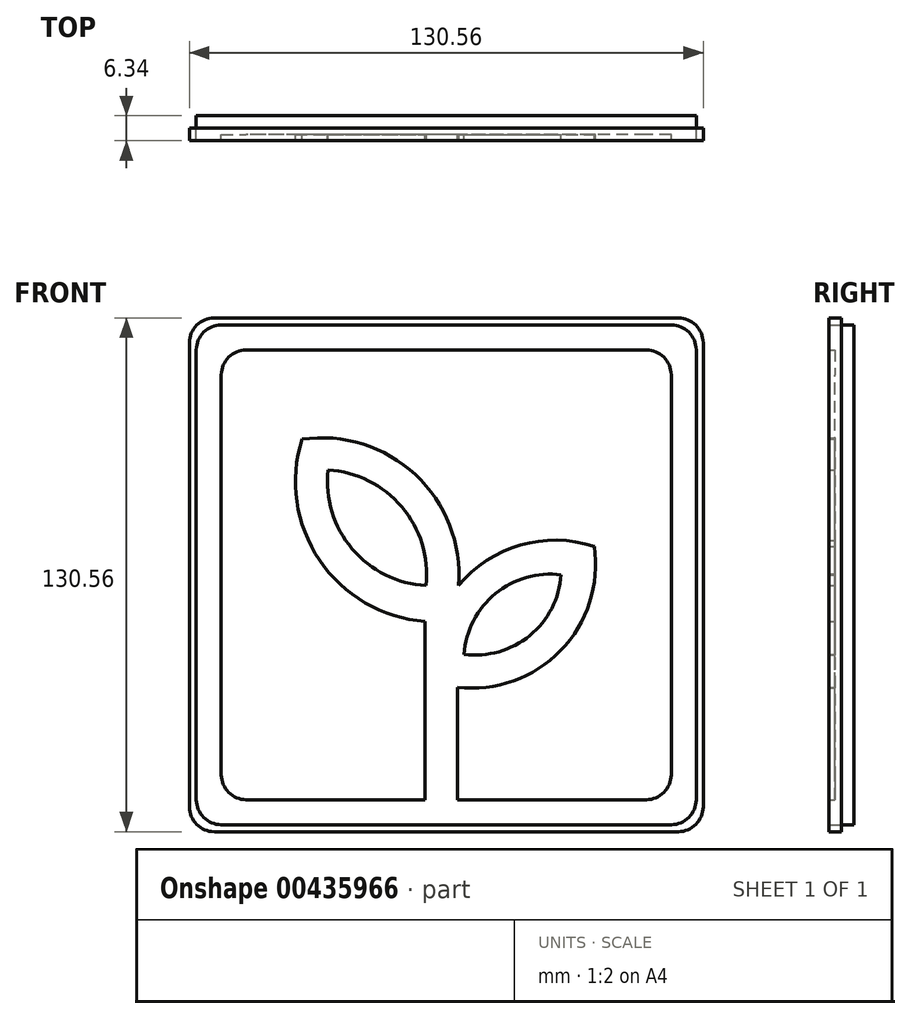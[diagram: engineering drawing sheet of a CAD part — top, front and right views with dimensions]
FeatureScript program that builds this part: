
annotation { "Feature Type Name" : "Feature", "Feature Type Description" : "" }
export const myFeature = defineFeature(function(context is Context, id is Id, definition is map)
    precondition{}
    {
        {
            var Q0;
            Q0=qCreatedBy(makeId("Front.planeOp"),FACE);
            var sketch = newSketch(context, id + "F0", { "sketchPlane" : qUnion([Q0])});
            skLineSegment(sketch, "E0", {"start": v(0, 67.9) * mm, "end": v(0, -67.43) * mm, "construction": true});
            skLineSegment(sketch, "E1", {"start": v(-68.62, 0) * mm, "end": v(68.14, 0) * mm, "construction": true});
            skLineSegment(sketch, "E2.bottom", {"start": v(-57.15, 63.5) * mm, "end": v(57.15, 63.5) * mm});
            skLineSegment(sketch, "E2.top", {"start": v(-57.15, -63.5) * mm, "end": v(57.15, -63.5) * mm});
            skLineSegment(sketch, "E2.left", {"start": v(-63.5, 57.15) * mm, "end": v(-63.5, -57.15) * mm});
            skLineSegment(sketch, "E2.right", {"start": v(63.5, 57.15) * mm, "end": v(63.5, -57.15) * mm});
            skPoint(sketch, "E3.visualSharp", {"position": v(-63.5, 63.5) * mm});
            skArc(sketch, "E3.filletArc", {"start": v(-57.15, 63.5) * mm, "mid": v(-61.64, 61.64) * mm, "end": v(-63.5, 57.15) * mm});
            skPoint(sketch, "E4.visualSharp", {"position": v(-63.5, -63.5) * mm});
            skArc(sketch, "E4.filletArc", {"start": v(-63.5, -57.15) * mm, "mid": v(-61.64, -61.64) * mm, "end": v(-57.15, -63.5) * mm});
            skPoint(sketch, "E5.visualSharp", {"position": v(63.5, -63.5) * mm});
            skArc(sketch, "E5.filletArc", {"start": v(57.15, -63.5) * mm, "mid": v(61.64, -61.64) * mm, "end": v(63.5, -57.15) * mm});
            skPoint(sketch, "E6.visualSharp", {"position": v(63.5, 63.5) * mm});
            skArc(sketch, "E6.filletArc", {"start": v(63.5, 57.15) * mm, "mid": v(61.64, 61.64) * mm, "end": v(57.15, 63.5) * mm});
            skSolve(sketch);
        }
        {
            var Q0;
            Q0=makeQuery(id+"F0.imprint","IMPRINT",FACE,{"disambiguationData":[TD([[makeQuery(id+"F0.imprint","IMPRINT",EDGE,{"derivedFrom":sQuery(id+"F0.wireOp",EDGE,"E2.bottom")}),-1.0]])]});
            var sketch = newSketch(context, id + "F1", { "sketchPlane" : qUnion([Q0])});
            skLineSegment(sketch, "E7", {"start": v(-5.39, -57.15) * mm, "end": v(-5.39, -11.84) * mm});
            skArc(sketch, "E8", {"start": v(4.55, -20.2) * mm, "mid": v(21.24, -15.43) * mm, "end": v(29.17, 0) * mm});
            skArc(sketch, "E9", {"start": v(29.17, 0) * mm, "mid": v(12.5, -4.79) * mm, "end": v(4.55, -20.2) * mm});
            skPoint(sketch, "E10", {"position": v(37.6, 7.23) * mm});
            skPoint(sketch, "E11", {"position": v(3.09, -2.73) * mm});
            skPoint(sketch, "E12", {"position": v(-5.1, -2.73) * mm});
            skPoint(sketch, "E13", {"position": v(-36.64, 34.45) * mm});
            skPoint(sketch, "E14", {"position": v(-30.02, 26.63) * mm});
            skArc(sketch, "E15", {"start": v(2.84, -28.56) * mm, "mid": v(29.07, -19.26) * mm, "end": v(37.6, 7.23) * mm});
            skArc(sketch, "E16", {"start": v(37.6, 7.23) * mm, "mid": v(18.83, 7.52) * mm, "end": v(3.09, -2.73) * mm});
            skArc(sketch, "E17", {"start": v(-5.1, -2.73) * mm, "mid": v(-11.3, 17.27) * mm, "end": v(-30.02, 26.63) * mm});
            skArc(sketch, "E18", {"start": v(-30.02, 26.63) * mm, "mid": v(-23.9, 6.59) * mm, "end": v(-5.1, -2.73) * mm});
            skArc(sketch, "E19", {"start": v(-36.64, 34.45) * mm, "mid": v(-32.21, 3.74) * mm, "end": v(-5.39, -11.84) * mm});
            skArc(sketch, "E20", {"start": v(3.09, -2.73) * mm, "mid": v(-7.83, 25.42) * mm, "end": v(-36.64, 34.45) * mm});
            skLineSegment(sketch, "E21.bottom", {"start": v(-50.8, 57.15) * mm, "end": v(50.8, 57.15) * mm});
            skLineSegment(sketch, "E21.top", {"start": v(-50.8, -57.15) * mm, "end": v(-5.39, -57.15) * mm});
            skLineSegment(sketch, "E21.left", {"start": v(-57.15, 50.8) * mm, "end": v(-57.15, -50.8) * mm});
            skLineSegment(sketch, "E21.right", {"start": v(57.15, 50.8) * mm, "end": v(57.15, -50.8) * mm});
            skArc(sketch, "E22.filletArc", {"start": v(-57.15, -50.8) * mm, "mid": v(-55.3, -55.3) * mm, "end": v(-50.8, -57.15) * mm});
            skPoint(sketch, "E23.visualSharp", {"position": v(-57.15, 57.15) * mm});
            skArc(sketch, "E23.filletArc", {"start": v(-50.8, 57.15) * mm, "mid": v(-55.3, 55.3) * mm, "end": v(-57.15, 50.8) * mm});
            skPoint(sketch, "E24.visualSharp", {"position": v(57.15, 57.15) * mm});
            skArc(sketch, "E24.filletArc", {"start": v(57.15, 50.8) * mm, "mid": v(55.3, 55.3) * mm, "end": v(50.8, 57.15) * mm});
            skArc(sketch, "E25.filletArc", {"start": v(50.8, -57.15) * mm, "mid": v(55.3, -55.3) * mm, "end": v(57.15, -50.8) * mm});
            skLineSegment(sketch, "E26", {"start": v(2.84, -28.56) * mm, "end": v(2.84, -57.15) * mm});
            skLineSegment(sketch, "E27.bottom", {"start": v(-58.93, 65.28) * mm, "end": v(58.93, 65.28) * mm});
            skLineSegment(sketch, "E27.top", {"start": v(-58.93, -65.28) * mm, "end": v(58.93, -65.28) * mm});
            skLineSegment(sketch, "E27.left", {"start": v(-65.28, 58.93) * mm, "end": v(-65.28, -58.93) * mm});
            skLineSegment(sketch, "E27.right", {"start": v(65.28, 58.93) * mm, "end": v(65.28, -58.93) * mm});
            skPoint(sketch, "E28.visualSharp", {"position": v(-65.28, 65.28) * mm});
            skArc(sketch, "E28.filletArc", {"start": v(-58.93, 65.28) * mm, "mid": v(-63.42, 63.42) * mm, "end": v(-65.28, 58.93) * mm});
            skPoint(sketch, "E29.visualSharp", {"position": v(-65.28, -65.28) * mm});
            skArc(sketch, "E29.filletArc", {"start": v(-65.28, -58.93) * mm, "mid": v(-63.42, -63.42) * mm, "end": v(-58.93, -65.28) * mm});
            skPoint(sketch, "E30.visualSharp", {"position": v(65.28, -65.28) * mm});
            skArc(sketch, "E30.filletArc", {"start": v(58.93, -65.28) * mm, "mid": v(63.42, -63.42) * mm, "end": v(65.28, -58.93) * mm});
            skPoint(sketch, "E31.visualSharp", {"position": v(65.28, 65.28) * mm});
            skArc(sketch, "E31.filletArc", {"start": v(65.28, 58.93) * mm, "mid": v(63.42, 63.42) * mm, "end": v(58.93, 65.28) * mm});
            skLineSegment(sketch, "E32.trimOffspring", {"start": v(2.84, -57.15) * mm, "end": v(50.8, -57.15) * mm});
            skSolve(sketch);
        }
        {
            var Q0;
            Q0 = qSketchRegion(id + "F0", true);
            extrude(context, id + "F2", {"entities" : qUnion([Q0]), "depth" : 1.65 * mm});
        }
        {
            var Q0;
            Q0 = qSketchRegion(id + "F1", true);
            extrude(context, id + "F3", {"entities" : qUnion([Q0]), "operationType" : NewBodyOperationType.ADD, "depth" : 3.17 * mm});
        }
        {
            var Q0;
            Q0=qSketchRegion(id+"F0",true);
            extrude(context, id + "F4", {"entities" : qUnion([Q0]), "endBound" : BoundingType.SYMMETRIC, "depth" : 6.35 * mm});
        }
    });
